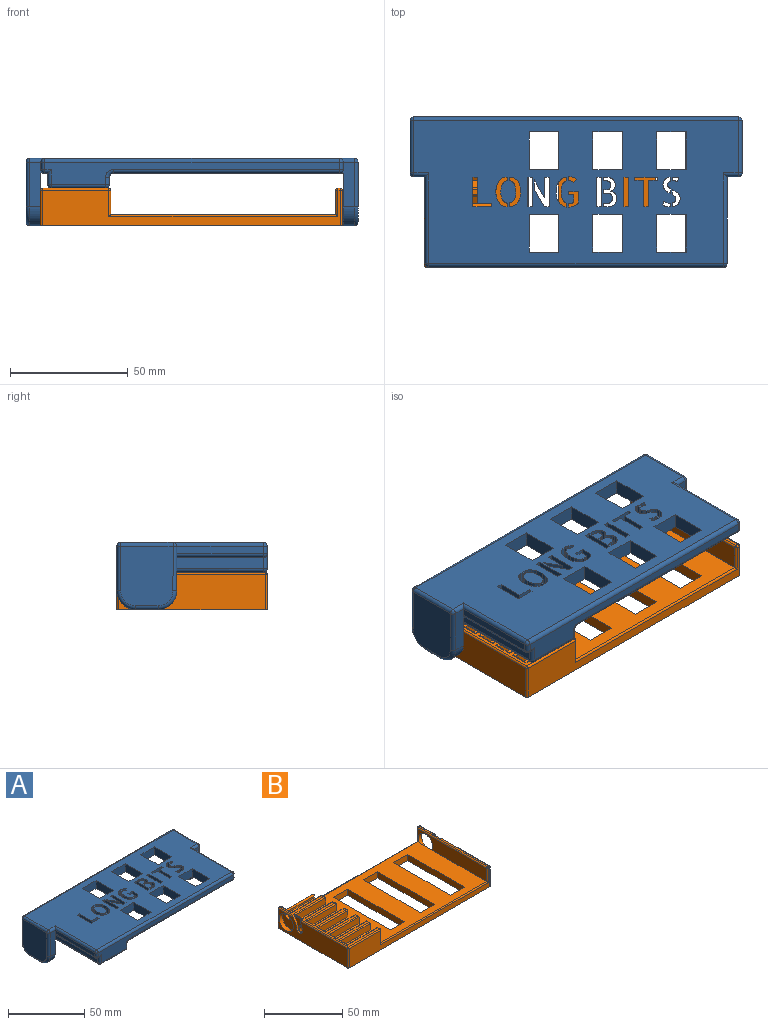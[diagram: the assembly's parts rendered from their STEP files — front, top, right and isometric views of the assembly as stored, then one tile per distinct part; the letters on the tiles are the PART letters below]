
ASSEMBLY  parts=2 mates=1
PART A: 304 faces, bbox 141x64.4x29.2 mm
  f0: plane 137.8x60.58mm, normal (0,0,1), area 6261.5mm2, adj f47,f48,f57,f58,f61,f64,f65,f66
  f1: plane 97.67x60.58mm, normal (0,0,-1), area 4295.3mm2, adj f4,f21,f26,f28,f70,f71,f73,f74
  f2: plane 57.78x23.02mm, normal (0,0,-1), area 1295.3mm2, adj f3,f13,f15,f17,f93,f94,f95,f96
  f3: cylinder r=1.59mm len=59.58mm, axis (0,1,0), area 145.3mm2, adj f2,f7,f12,f15,f18,f96,f97,f98
  f4: cylinder r=1.59mm len=60.58mm, axis (0,1,0), area 148.8mm2, adj f1,f7,f20,f72,f89,f90,f91,f92
  f5: plane 36.77x3.18mm, normal (1,0,0), area 116.7mm2, adj f28,f66,f68,f70
  f6: plane 36.77x3.18mm, normal (-1,0,0), area 116.7mm2, adj f25,f52,f60,f61
  f7: plane 61.05x3.18mm, normal (1,0,0), area 191.7mm2, adj f3,f4,f12,f19,f72
  f8: plane 62.17x2.86mm, normal (0,0,-1), area 119.3mm2, adj f9,f11,f22,f25,f51,f52
  f9: plane 137.8x19.05mm, normal (0,1,0), area 634.3mm2, adj f8,f12,f22,f26,f37,f38,f42,f48
  f10: plane 125.1x9.53mm, normal (0,-1,0), area 545.5mm2, adj f14,f17,f19,f20,f21,f51,f60,f65
  f11: plane 62.17x4.76mm, normal (-1,0,0), area 289.9mm2, adj f8,f12,f13,f14
  f12: plane 26.21x5.53mm, normal (0,0.88,-0.48), area 163.6mm2, adj f3,f7,f9,f11,f13,f15,f72
  f13: cylinder r=1.59mm len=59.58mm, axis (0,-1,0), area 146.7mm2, adj f2,f11,f12,f15,f16
  f14: cylinder r=1.59mm len=6.35mm, axis (0,0,-1), area 13.3mm2, adj f10,f11,f16,f51
  f15: cylinder r=1.59mm len=25.81mm, axis (-1,0,0), area 41.9mm2, adj f2,f3,f12,f13
  f16: sphere r=1.59mm, area 4mm2, adj f13,f14,f17
  f17: cylinder r=1.59mm len=23.02mm, axis (1,0,0), area 57.4mm2, adj f2,f10,f16,f18
  f18: sphere r=1.59mm, area 4mm2, adj f3,f17,f19
  f19: cylinder r=1.59mm len=3.18mm, axis (0,0,1), area 7.9mm2, adj f7,f10,f18,f20
  f20: torus R=3.17mm, axis (0,1,0), area 8.5mm2, adj f4,f10,f19,f21
  f21: cylinder r=1.59mm len=96.05mm, axis (1,0,0), area 239.5mm2, adj f1,f10,f20,f69
  f22: plane 25.4x22.23mm, normal (1,0,0), area 400.5mm2, adj f8,f9,f23,f25,f30,f32,f38,f39
  f23: plane 9.53x4.76mm, normal (0,0,-1), area 45.4mm2, adj f22,f38,f39,f41
  f24: plane 25.4x22.23mm, normal (-1,0,0), area 547.2mm2, adj f40,f41,f42,f43,f46,f47
  f25: plane 19.05x6.35mm, normal (0,-1,0), area 91.3mm2, adj f6,f8,f22,f39,f46,f52,f57
  f26: plane 25.4x23.81mm, normal (-1,0,0), area 401mm2, adj f1,f9,f27,f28,f33,f35,f36,f37
  f27: plane 9.53x4.76mm, normal (0,0,-1), area 45.4mm2, adj f26,f36,f37,f50
  f28: plane 19.05x6.35mm, normal (0,-1,0), area 91.3mm2, adj f1,f5,f26,f36,f59,f64,f70
  f29: plane 25.4x22.23mm, normal (1,0,0), area 547.2mm2, adj f45,f49,f50,f55,f58,f59
  f30: cylinder r=6.1mm len=12.19mm, axis (-1,0,0), area 107mm2, adj f22,f31
  f31: plane 12.19x12.19mm, normal (1,0,0), area 116.7mm2, adj f30
  f32: sphere r=2.54mm, area 40.5mm2, adj f22
  f33: cylinder r=6.1mm len=12.19mm, axis (1,0,0), area 107mm2, adj f26,f34
  f34: plane 12.19x12.19mm, normal (-1,0,0), area 116.7mm2, adj f33
  f35: sphere r=2.54mm, area 40.5mm2, adj f26
  f36: cylinder r=7.94mm len=7.94mm, axis (1,0,0), area 59.4mm2, adj f26,f27,f28,f55
  f37: cylinder r=7.94mm len=7.94mm, axis (1,0,0), area 59.4mm2, adj f9,f26,f27,f45
  f38: cylinder r=7.94mm len=7.94mm, axis (-1,0,0), area 59.4mm2, adj f9,f22,f23,f40
  f39: cylinder r=7.94mm len=7.94mm, axis (1,0,0), area 59.4mm2, adj f22,f23,f25,f43
  f40: torus R=6.35mm, axis (-1,0,0), area 28.8mm2, adj f24,f38,f41,f42
  f41: cylinder r=1.59mm len=9.53mm, axis (0,-1,0), area 23.8mm2, adj f23,f24,f40,f43
  f42: cylinder r=1.59mm len=19.05mm, axis (0,0,1), area 47.5mm2, adj f9,f24,f40,f44
  f43: torus R=6.35mm, axis (-1,0,0), area 28.8mm2, adj f24,f39,f41,f46
  f44: sphere r=1.59mm, area 4mm2, adj f42,f47,f48
  f45: torus R=6.35mm, axis (-1,0,0), area 28.8mm2, adj f29,f37,f49,f50
  f46: cylinder r=1.59mm len=19.05mm, axis (0,0,-1), area 47.5mm2, adj f24,f25,f43,f53
  f47: cylinder r=1.59mm len=22.23mm, axis (0,-1,0), area 55.4mm2, adj f0,f24,f44,f53
  f48: cylinder r=1.59mm len=137.8mm, axis (1,0,0), area 343.6mm2, adj f0,f9,f44,f54
  f49: cylinder r=1.59mm len=19.05mm, axis (0,0,-1), area 47.5mm2, adj f9,f29,f45,f54
  f50: cylinder r=1.59mm len=9.53mm, axis (0,1,0), area 23.8mm2, adj f27,f29,f45,f55
  f51: cylinder r=1.59mm len=2.86mm, axis (1,0,0), area 4.6mm2, adj f8,f10,f14,f56
  f52: cylinder r=1.59mm len=36.77mm, axis (0,-1,0), area 91.7mm2, adj f6,f8,f25,f56
  f53: sphere r=1.59mm, area 4mm2, adj f46,f47,f57
  f54: sphere r=1.59mm, area 4mm2, adj f48,f49,f58
  f55: torus R=6.35mm, axis (-1,0,0), area 28.8mm2, adj f29,f36,f50,f59
  f56: sphere r=1.59mm, area 4mm2, adj f51,f52,f60
  f57: cylinder r=1.59mm len=6.35mm, axis (1,0,0), area 13.3mm2, adj f0,f25,f53,f61
  f58: cylinder r=1.59mm len=22.23mm, axis (0,1,0), area 55.4mm2, adj f0,f29,f54,f62
  f59: cylinder r=1.59mm len=19.05mm, axis (0,0,-1), area 47.5mm2, adj f28,f29,f55,f62
  f60: cylinder r=1.59mm len=3.18mm, axis (0,0,-1), area 7.9mm2, adj f6,f10,f56,f63
  f61: cylinder r=1.59mm len=38.35mm, axis (0,1,0), area 93.1mm2, adj f0,f6,f57,f63
  f62: sphere r=1.59mm, area 4mm2, adj f58,f59,f64
  f63: sphere r=1.59mm, area 4mm2, adj f60,f61,f65
  f64: cylinder r=1.59mm len=6.35mm, axis (1,0,0), area 13.3mm2, adj f0,f28,f62,f66
  f65: cylinder r=1.59mm len=125.1mm, axis (-1,0,0), area 312mm2, adj f0,f10,f63,f67
  f66: cylinder r=1.59mm len=38.35mm, axis (0,-1,0), area 93.1mm2, adj f0,f5,f64,f67
  f67: sphere r=1.59mm, area 4mm2, adj f65,f66,f68
  f68: cylinder r=1.59mm len=3.18mm, axis (0,0,1), area 7.9mm2, adj f5,f10,f67,f69
  f69: sphere r=1.59mm, area 4mm2, adj f21,f68,f70
  f70: cylinder r=1.59mm len=36.77mm, axis (0,1,0), area 91.7mm2, adj f1,f5,f28,f69
  f71: cylinder r=1.59mm len=97.64mm, axis (-1,0,0), area 243.5mm2, adj f1,f9,f26,f72
  f72: torus R=3.17mm, axis (0,1,0), area 6.8mm2, adj f4,f7,f9,f12,f71
  f73: extruded ~6.35x1.58mm, area 12.9mm2, adj f0,f1,f74,f89
  f74: extruded ~6.35x1.29mm, area 8.6mm2, adj f0,f1,f73,f75
  f75: plane 6.35x0.68mm, normal (0,1,0), area 4.3mm2, adj f0,f1,f74,f76
  f76: plane 6.35x1.62mm, normal (-1,0,0), area 10.3mm2, adj f0,f1,f75,f77
  f77: extruded ~6.35x1.08mm, area 7.3mm2, adj f0,f1,f76,f78
  f78: extruded ~6.35x0.9mm, area 8.1mm2, adj f0,f1,f77,f79
  f79: extruded ~6.35x1.46mm, area 10.1mm2, adj f0,f1,f78,f80
  f80: extruded ~6.35x2.09mm, area 13.4mm2, adj f0,f1,f79,f81
  f81: extruded ~6.35x2.09mm, area 13.4mm2, adj f0,f1,f80,f82
  f82: extruded ~6.35x1.45mm, area 10mm2, adj f0,f1,f81,f83
  f83: extruded ~6.35x0.9mm, area 8mm2, adj f0,f1,f82,f84
  f84: extruded ~6.35x1.1mm, area 7.4mm2, adj f0,f1,f83,f85
  f85: plane 6.35x1.54mm, normal (-1,0,0), area 9.8mm2, adj f0,f1,f84,f86
  f86: plane 6.35x1.11mm, normal (0,-1,0), area 7.1mm2, adj f0,f1,f85,f87
  f87: extruded ~6.35x0.86mm, area 5.8mm2, adj f0,f1,f86,f88
  f88: extruded ~6.35x1.57mm, area 12.9mm2, adj f0,f1,f87,f90
  f89: extruded ~6.36x2.01mm, area 14.4mm2, adj f0,f1,f4,f73,f92
  f90: extruded ~6.36x2mm, area 14.4mm2, adj f0,f1,f4,f88,f91
  f91: extruded ~6.44x2.71mm, area 17.6mm2, adj f0,f4,f90,f92
  f92: extruded ~6.44x2.72mm, area 17.7mm2, adj f0,f4,f89,f91
  f93: plane 12.7x11.13mm, normal (-1,0,0), area 141.3mm2, adj f0,f2,f94,f97
  f94: plane 12.7x2.1mm, normal (0,-1,0), area 26.7mm2, adj f0,f2,f93,f95
  f95: plane 12.7x12.69mm, normal (1,0,0), area 161.2mm2, adj f0,f2,f94,f96
  f96: plane 12.7x7.94mm, normal (0,1,0), area 100.8mm2, adj f0,f2,f3,f95,f98
  f97: plane 12.7x5.84mm, normal (0,-1,0), area 74.1mm2, adj f0,f2,f3,f93,f98
  f98: plane 12.48x1.57mm, normal (-1,0,0), area 19.6mm2, adj f0,f3,f96,f97
  f99: plane 12.69x6.35mm, normal (-1,0,0), area 80.6mm2, adj f0,f1,f100,f105
  f100: plane 6.35x2.1mm, normal (0,-1,0), area 13.3mm2, adj f0,f1,f99,f101
  f101: plane 8.75x6.35mm, normal (1,0,0), area 55.6mm2, adj f0,f1,f100,f102
  f102: plane 7.53x6.35mm, normal (-0.87,-0.49,0), area 55mm2, adj f0,f1,f101,f103
  f103: plane 6.35x3.96mm, normal (1,0,0), area 25.2mm2, adj f0,f1,f102,f104
  f104: plane 7.51x6.35mm, normal (0.87,0.49,0), area 54.9mm2, adj f0,f1,f103,f105
  f105: plane 6.35x2.1mm, normal (0,1,0), area 13.3mm2, adj f0,f1,f99,f104
  f106: extruded ~6.35x0.43mm, area 2.7mm2, adj f0,f1,f107,f144
  f107: extruded ~6.35x0.75mm, area 4.9mm2, adj f0,f1,f106,f108
  f108: extruded ~6.35x0.88mm, area 6mm2, adj f0,f1,f107,f109
  f109: extruded ~6.35x0.84mm, area 6.7mm2, adj f0,f1,f108,f110
  f110: extruded ~6.35x1.03mm, area 7.7mm2, adj f0,f1,f109,f111
  f111: extruded ~6.35x1.48mm, area 9.6mm2, adj f0,f1,f110,f112
  f112: extruded ~6.35x1.25mm, area 8.2mm2, adj f0,f1,f111,f113
  f113: extruded ~6.35x0.92mm, area 7.2mm2, adj f0,f1,f112,f114
  f114: extruded ~6.35x0.84mm, area 6.5mm2, adj f0,f1,f113,f115
  f115: extruded ~6.35x0.84mm, area 5.6mm2, adj f0,f1,f114,f116
  f116: extruded ~6.35x0.65mm, area 4.5mm2, adj f0,f1,f115,f117
  f117: extruded ~6.35x0.59mm, area 5.1mm2, adj f0,f1,f116,f118
  f118: extruded ~6.35x0.77mm, area 5.6mm2, adj f0,f1,f117,f119
  f119: extruded ~6.35x0.97mm, area 6.3mm2, adj f0,f1,f118,f120
  f120: extruded ~6.35x1.58mm, area 10.4mm2, adj f0,f1,f119,f121
  f121: extruded ~6.35x1.08mm, area 9.1mm2, adj f0,f1,f120,f122
  f122: extruded ~6.35x1.34mm, area 9.4mm2, adj f0,f1,f121,f123
  f123: extruded ~6.35x1.57mm, area 10.1mm2, adj f0,f1,f122,f124
  f124: plane 6.35x0.88mm, normal (0,-1,0), area 5.6mm2, adj f0,f1,f123,f125
  f125: plane 6.35x1.57mm, normal (1,0,0), area 9.9mm2, adj f0,f1,f124,f126
  f126: plane 6.35x0.67mm, normal (0,1,0), area 4.3mm2, adj f0,f1,f125,f127
  f127: extruded ~6.35x1.28mm, area 8.2mm2, adj f0,f1,f126,f128
  f128: extruded ~6.35x0.74mm, area 5.5mm2, adj f0,f1,f127,f129
  f129: extruded ~6.35x0.61mm, area 4.5mm2, adj f0,f1,f128,f130
  f130: extruded ~6.35x0.65mm, area 4.2mm2, adj f0,f1,f129,f131
  f131: extruded ~6.35x1.19mm, area 7.7mm2, adj f0,f1,f130,f132
  f132: extruded ~6.35x0.59mm, area 5.2mm2, adj f0,f1,f131,f133
  f133: extruded ~6.35x0.74mm, area 4.9mm2, adj f0,f1,f132,f134
  f134: extruded ~6.35x0.78mm, area 4.9mm2, adj f0,f1,f133,f135
  f135: plane 6.35x0.83mm, normal (0,-1,0), area 5.3mm2, adj f0,f1,f134,f136
  f136: plane 6.35x1.4mm, normal (1,0,0), area 8.9mm2, adj f0,f1,f135,f137
  f137: plane 6.35x1.72mm, normal (0,1,0), area 10.9mm2, adj f0,f1,f136,f138
  f138: extruded ~6.35x1.57mm, area 11.1mm2, adj f0,f1,f137,f139
  f139: extruded ~6.35x1.57mm, area 10.7mm2, adj f0,f1,f138,f140
  f140: extruded ~6.35x1.57mm, area 10.7mm2, adj f0,f1,f139,f141
  f141: extruded ~6.35x1.43mm, area 10.1mm2, adj f0,f1,f140,f142
  f142: plane 6.35x1.88mm, normal (0,-1,0), area 11.9mm2, adj f0,f1,f141,f143
  f143: plane 6.35x1.52mm, normal (1,0,0), area 9.6mm2, adj f0,f1,f142,f144
  f144: plane 6.35x2mm, normal (0,1,0), area 12.7mm2, adj f0,f1,f106,f143
  f145: extruded ~6.35x0.89mm, area 7.7mm2, adj f0,f1,f146,f159
  f146: plane 6.35x4.91mm, normal (-1,0,0), area 31.2mm2, adj f0,f1,f145,f147
  f147: plane 6.35x4.2mm, normal (0,-1,0), area 26.7mm2, adj f0,f1,f146,f148
  f148: plane 6.35x1.41mm, normal (1,0,0), area 9mm2, adj f0,f1,f147,f149
  f149: plane 6.35x2.16mm, normal (0,1,0), area 13.7mm2, adj f0,f1,f148,f150
  f150: plane 6.35x3.14mm, normal (1,0,0), area 19.9mm2, adj f0,f1,f149,f151
  f151: extruded ~6.35x0.42mm, area 3.3mm2, adj f0,f1,f150,f152
  f152: extruded ~6.35x0.6mm, area 4mm2, adj f0,f1,f151,f153
  f153: extruded ~6.35x0.62mm, area 4mm2, adj f0,f1,f152,f154
  f154: extruded ~6.35x0.51mm, area 3.2mm2, adj f0,f1,f153,f155
  f155: plane 6.35x1.52mm, normal (1,0,0), area 9.6mm2, adj f0,f1,f154,f156
  f156: plane 6.35x0.02mm, normal (0,1,0), area 0.1mm2, adj f0,f1,f155,f157
  f157: extruded ~6.35x1.15mm, area 7.3mm2, adj f0,f1,f156,f158
  f158: extruded ~6.35x1.12mm, area 7.4mm2, adj f0,f1,f157,f159
  f159: extruded ~6.35x1.03mm, area 7.4mm2, adj f0,f1,f145,f158
  f160: extruded ~6.35x1.4mm, area 9.5mm2, adj f0,f1,f161,f179
  f161: extruded ~6.35x0.9mm, area 7.6mm2, adj f0,f1,f160,f162
  f162: extruded ~6.35x0.96mm, area 6.8mm2, adj f0,f1,f161,f163
  f163: plane 6.35x1.59mm, normal (-1,0,0), area 10.1mm2, adj f0,f1,f162,f164
  f164: plane 6.35x0.7mm, normal (0,-1,0), area 4.4mm2, adj f0,f1,f163,f165
  f165: extruded ~6.35x1.13mm, area 7.7mm2, adj f0,f1,f164,f166
  f166: extruded ~6.35x1.45mm, area 12.3mm2, adj f0,f1,f165,f167
  f167: extruded ~6.35x1.95mm, area 13.8mm2, adj f0,f1,f166,f168
  f168: extruded ~6.35x2.63mm, area 16.9mm2, adj f0,f1,f167,f169
  f169: extruded ~6.35x2.63mm, area 16.9mm2, adj f0,f1,f168,f170
  f170: extruded ~6.35x1.96mm, area 13.9mm2, adj f0,f1,f169,f171
  f171: extruded ~6.35x1.45mm, area 12.4mm2, adj f0,f1,f170,f172
  f172: extruded ~6.35x1.49mm, area 10.1mm2, adj f0,f1,f171,f173
  f173: extruded ~6.35x0.33mm, area 2.2mm2, adj f0,f1,f172,f174
  f174: plane 6.35x1.57mm, normal (-1,0,0), area 10mm2, adj f0,f1,f173,f175
  f175: extruded ~6.35x0.96mm, area 6.9mm2, adj f0,f1,f174,f176
  f176: extruded ~6.35x0.97mm, area 7.9mm2, adj f0,f1,f175,f177
  f177: extruded ~6.35x1.46mm, area 9.9mm2, adj f0,f1,f176,f178
  f178: extruded ~6.35x1.96mm, area 12.6mm2, adj f0,f1,f177,f179
  f179: extruded ~6.35x1.94mm, area 12.4mm2, adj f0,f1,f160,f178
  f180: plane 6.35x1.7mm, normal (1,0,0), area 10.8mm2, adj f0,f1,f181,f188
  f181: plane 6.35x0.07mm, normal (0,1,0), area 0.4mm2, adj f0,f1,f180,f182
  f182: extruded ~6.35x1.1mm, area 7.2mm2, adj f0,f1,f181,f183
  f183: extruded ~6.35x0.95mm, area 7.6mm2, adj f0,f1,f182,f184
  f184: plane 6.35x1.43mm, normal (-0.66,0.75,0), area 12.2mm2, adj f0,f1,f183,f185
  f185: extruded ~6.35x1.6mm, area 12.2mm2, adj f0,f1,f184,f186
  f186: extruded ~6.35x0.43mm, area 2.9mm2, adj f0,f1,f185,f187
  f187: extruded ~6.35x1.5mm, area 9.6mm2, adj f0,f1,f186,f188
  f188: plane 6.35x0.02mm, normal (0,-1,0), area 0.1mm2, adj f0,f1,f180,f187
  f189: plane 12.69x6.35mm, normal (1,0,0), area 80.6mm2, adj f0,f1,f190,f192
  f190: plane 6.35x2.1mm, normal (0,1,0), area 13.4mm2, adj f0,f1,f189,f191
  f191: plane 12.69x6.35mm, normal (-1,0,0), area 80.6mm2, adj f0,f1,f190,f192
  f192: plane 6.35x2.1mm, normal (0,-1,0), area 13.4mm2, adj f0,f1,f189,f191
  f193: extruded ~6.35x1.1mm, area 7.4mm2, adj f0,f1,f194,f212
  f194: plane 6.35x1.62mm, normal (1,0,0), area 10.3mm2, adj f0,f1,f193,f195
  f195: plane 6.35x0.68mm, normal (0,1,0), area 4.3mm2, adj f0,f1,f194,f196
  f196: extruded ~6.35x1.28mm, area 8.6mm2, adj f0,f1,f195,f197
  f197: extruded ~6.35x1.56mm, area 12.8mm2, adj f0,f1,f196,f198
  f198: extruded ~6.35x2.01mm, area 14.4mm2, adj f0,f1,f197,f199
  f199: extruded ~6.35x2.72mm, area 17.5mm2, adj f0,f1,f198,f200
  f200: extruded ~6.35x2.71mm, area 17.5mm2, adj f0,f1,f199,f201
  f201: extruded ~6.35x2mm, area 14.4mm2, adj f0,f1,f200,f202
  f202: extruded ~6.35x1.57mm, area 12.9mm2, adj f0,f1,f201,f203
  f203: extruded ~6.35x0.82mm, area 5.6mm2, adj f0,f1,f202,f204
  f204: plane 6.35x1.14mm, normal (0,-1,0), area 7.2mm2, adj f0,f1,f203,f205
  f205: plane 6.35x1.52mm, normal (1,0,0), area 9.7mm2, adj f0,f1,f204,f206
  f206: extruded ~6.35x1.08mm, area 7.3mm2, adj f0,f1,f205,f207
  f207: extruded ~6.35x0.91mm, area 8.1mm2, adj f0,f1,f206,f208
  f208: extruded ~6.35x1.45mm, area 10mm2, adj f0,f1,f207,f209
  f209: extruded ~6.35x2.09mm, area 13.4mm2, adj f0,f1,f208,f210
  f210: extruded ~6.35x2.09mm, area 13.4mm2, adj f0,f1,f209,f211
  f211: extruded ~6.35x1.45mm, area 10mm2, adj f0,f1,f210,f212
  f212: extruded ~6.35x0.9mm, area 8mm2, adj f0,f1,f193,f211
  f213: extruded ~6.35x1.02mm, area 8.3mm2, adj f0,f1,f214,f226
  f214: extruded ~6.35x1.08mm, area 8.2mm2, adj f0,f1,f213,f215
  f215: extruded ~6.35x1.16mm, area 8.2mm2, adj f0,f1,f214,f216
  f216: plane 6.35x2.02mm, normal (1,0,0), area 12.8mm2, adj f0,f1,f215,f217
  f217: extruded ~6.35x1.02mm, area 8mm2, adj f0,f1,f216,f218
  f218: extruded ~6.35x1mm, area 7mm2, adj f0,f1,f217,f219
  f219: extruded ~6.35x1.88mm, area 16.3mm2, adj f0,f1,f218,f220
  f220: plane 6.35x1.64mm, normal (1,0,0), area 10.4mm2, adj f0,f1,f219,f221
  f221: plane 6.35x0.12mm, normal (0,1,0), area 0.7mm2, adj f0,f1,f220,f222
  f222: extruded ~6.35x1.29mm, area 8.7mm2, adj f0,f1,f221,f223
  f223: extruded ~6.35x1.04mm, area 8.4mm2, adj f0,f1,f222,f224
  f224: extruded ~6.35x1.06mm, area 8mm2, adj f0,f1,f223,f225
  f225: extruded ~6.35x1.21mm, area 7.8mm2, adj f0,f1,f224,f226
  f226: extruded ~6.35x1.5mm, area 9.8mm2, adj f0,f1,f213,f225
  f227: extruded ~6.35x0.91mm, area 7.3mm2, adj f0,f1,f228,f241
  f228: plane 6.35x1.66mm, normal (-1,0,0), area 10.5mm2, adj f0,f1,f227,f229
  f229: plane 6.35x0.71mm, normal (0,-1,0), area 4.5mm2, adj f0,f1,f228,f230
  f230: extruded ~6.35x0.54mm, area 3.7mm2, adj f0,f1,f229,f231
  f231: extruded ~6.35x1.03mm, area 8.1mm2, adj f0,f1,f230,f232
  f232: extruded ~6.35x1.06mm, area 8.1mm2, adj f0,f1,f231,f233
  f233: extruded ~6.35x1.36mm, area 8.9mm2, adj f0,f1,f232,f234
  f234: extruded ~6.35x1.36mm, area 8.9mm2, adj f0,f1,f233,f235
  f235: extruded ~6.35x1mm, area 8mm2, adj f0,f1,f234,f236
  f236: extruded ~6.35x1.03mm, area 8.1mm2, adj f0,f1,f235,f237
  f237: extruded ~6.35x1.14mm, area 8.2mm2, adj f0,f1,f236,f238
  f238: plane 6.35x1.97mm, normal (-1,0,0), area 12.5mm2, adj f0,f1,f237,f239
  f239: extruded ~6.35x0.91mm, area 7.4mm2, adj f0,f1,f238,f240
  f240: extruded ~6.35x1.09mm, area 7.4mm2, adj f0,f1,f239,f241
  f241: extruded ~6.35x0.96mm, area 6.6mm2, adj f0,f1,f227,f240
  f242: extruded ~6.35x0.49mm, area 3.5mm2, adj f0,f1,f243,f252
  f243: extruded ~6.35x1.08mm, area 7.4mm2, adj f0,f1,f242,f244
  f244: plane 6.35x1.73mm, normal (0,-1,0), area 11mm2, adj f0,f1,f243,f245
  f245: plane 6.35x1.54mm, normal (1,0,0), area 9.8mm2, adj f0,f1,f244,f246
  f246: extruded ~6.35x0.88mm, area 5.6mm2, adj f0,f1,f245,f247
  f247: extruded ~6.35x0.57mm, area 3.7mm2, adj f0,f1,f246,f248
  f248: extruded ~6.35x0.34mm, area 2.4mm2, adj f0,f1,f247,f249
  f249: extruded ~6.35x0.21mm, area 1.5mm2, adj f0,f1,f248,f250
  f250: extruded ~6.35x0.17mm, area 1.3mm2, adj f0,f1,f249,f251
  f251: extruded ~6.35x0.39mm, area 2.8mm2, adj f0,f1,f250,f252
  f252: extruded ~6.35x0.5mm, area 3.6mm2, adj f0,f1,f242,f251
  f253: extruded ~6.35x0.79mm, area 5.2mm2, adj f0,f1,f254,f263
  f254: extruded ~6.35x0.77mm, area 5.1mm2, adj f0,f1,f253,f255
  f255: extruded ~6.35x0.61mm, area 4.2mm2, adj f0,f1,f254,f256
  f256: plane 6.35x1.48mm, normal (0.97,-0.24,0), area 9.7mm2, adj f0,f1,f255,f257
  f257: extruded ~6.35x0.7mm, area 5.3mm2, adj f0,f1,f256,f258
  f258: extruded ~6.35x0.85mm, area 5.7mm2, adj f0,f1,f257,f259
  f259: extruded ~6.35x0.66mm, area 4.3mm2, adj f0,f1,f258,f260
  f260: plane 6.35x1.12mm, normal (0,1,0), area 7.1mm2, adj f0,f1,f259,f261
  f261: plane 6.35x1.57mm, normal (-1,0,0), area 10mm2, adj f0,f1,f260,f262
  f262: plane 6.35x0.05mm, normal (0,-1,0), area 0.3mm2, adj f0,f1,f261,f263
  f263: extruded ~6.35x0.74mm, area 4.7mm2, adj f0,f1,f253,f262
  f264: plane 11.28x6.35mm, normal (-1,0,0), area 71.6mm2, adj f0,f1,f265,f271
  f265: plane 6.35x3.79mm, normal (0,1,0), area 24.1mm2, adj f0,f1,f264,f266
  f266: plane 6.35x1.41mm, normal (-1,0,0), area 9mm2, adj f0,f1,f265,f267
  f267: plane 9.66x6.35mm, normal (0,-1,0), area 61.4mm2, adj f0,f1,f266,f268
  f268: plane 6.35x1.41mm, normal (1,0,0), area 9mm2, adj f0,f1,f267,f269
  f269: plane 6.35x3.79mm, normal (0,1,0), area 24.1mm2, adj f0,f1,f268,f270
  f270: plane 11.28x6.35mm, normal (1,0,0), area 71.6mm2, adj f0,f1,f269,f271
  f271: plane 6.35x2.08mm, normal (0,1,0), area 13.2mm2, adj f0,f1,f264,f270
  f272: plane 6.35x2.1mm, normal (0,1,0), area 13.3mm2, adj f0,f1,f273,f275
  f273: plane 12.69x6.35mm, normal (-1,0,0), area 80.6mm2, adj f0,f1,f272,f274
  f274: plane 6.35x2.1mm, normal (0,-1,0), area 13.3mm2, adj f0,f1,f273,f275
  f275: plane 12.69x6.35mm, normal (1,0,0), area 80.6mm2, adj f0,f1,f272,f274
  f276: plane 12.69x6.35mm, normal (-1,0,0), area 80.6mm2, adj f0,f1,f277,f279
  f277: plane 6.35x2.07mm, normal (0,-1,0), area 13.1mm2, adj f0,f1,f276,f278
  f278: plane 12.69x6.35mm, normal (1,0,0), area 80.6mm2, adj f0,f1,f277,f279
  f279: plane 6.35x2.07mm, normal (0,1,0), area 13.1mm2, adj f0,f1,f276,f278
  f280: plane 16.01x6.35mm, normal (-1,0,0), area 101.6mm2, adj f0,f1,f281,f283
  f281: plane 12.7x6.35mm, normal (0,-1,0), area 80.6mm2, adj f0,f1,f280,f282
  f282: plane 16.01x6.35mm, normal (1,0,0), area 101.6mm2, adj f0,f1,f281,f283
  f283: plane 12.7x6.35mm, normal (0,1,0), area 80.6mm2, adj f0,f1,f280,f282
  f284: plane 12.7x6.35mm, normal (0,-1,0), area 80.6mm2, adj f0,f1,f285,f287
  f285: plane 16.01x6.35mm, normal (1,0,0), area 101.6mm2, adj f0,f1,f284,f286
  f286: plane 12.7x6.35mm, normal (0,1,0), area 80.6mm2, adj f0,f1,f285,f287
  f287: plane 16.01x6.35mm, normal (-1,0,0), area 101.6mm2, adj f0,f1,f284,f286
  f288: plane 16.01x6.35mm, normal (-1,0,0), area 101.6mm2, adj f0,f1,f289,f291
  f289: plane 12.7x6.35mm, normal (0,-1,0), area 80.6mm2, adj f0,f1,f288,f290
  f290: plane 16.01x6.35mm, normal (1,0,0), area 101.6mm2, adj f0,f1,f289,f291
  f291: plane 12.7x6.35mm, normal (0,1,0), area 80.6mm2, adj f0,f1,f288,f290
  f292: plane 12.7x6.35mm, normal (0,-1,0), area 80.6mm2, adj f0,f1,f293,f295
  f293: plane 16x6.35mm, normal (1,0,0), area 101.6mm2, adj f0,f1,f292,f294
  f294: plane 12.7x6.35mm, normal (0,1,0), area 80.6mm2, adj f0,f1,f293,f295
  f295: plane 16x6.35mm, normal (-1,0,0), area 101.6mm2, adj f0,f1,f292,f294
  f296: plane 12.7x6.35mm, normal (0,1,0), area 80.6mm2, adj f0,f1,f297,f299
  f297: plane 16x6.35mm, normal (-1,0,0), area 101.6mm2, adj f0,f1,f296,f298
  f298: plane 12.7x6.35mm, normal (0,-1,0), area 80.6mm2, adj f0,f1,f297,f299
  f299: plane 16x6.35mm, normal (1,0,0), area 101.6mm2, adj f0,f1,f296,f298
  f300: plane 16x6.35mm, normal (-1,0,0), area 101.6mm2, adj f0,f1,f301,f303
  f301: plane 12.7x6.35mm, normal (0,-1,0), area 80.6mm2, adj f0,f1,f300,f302
  f302: plane 16x6.35mm, normal (1,0,0), area 101.6mm2, adj f0,f1,f301,f303
  f303: plane 12.7x6.35mm, normal (0,1,0), area 80.6mm2, adj f0,f1,f300,f302
PART B: 120 faces, bbox 128.3x63.8x15.9 mm
  f0: plane 62.17x28.26mm, normal (0,0,1), area 376.7mm2, adj f14,f15,f17,f84,f88,f90,f91,f92
  f1: plane 26.8x1.36mm, normal (0,-1,0), area 36.4mm2, adj f2,f10,f45,f119
  f2: plane 62.96x11.11mm, normal (1,0,0), area 403.6mm2, adj f1,f4,f13,f27,f29,f30,f32,f33
  f3: plane 128.28x63.75mm, normal (0,0,-1), area 6232.4mm2, adj f8,f11,f12,f13,f56,f57,f58,f59
  f4: plane 95.57x62.17mm, normal (0,0,1), area 3994.2mm2, adj f2,f5,f6,f28,f56,f57,f58,f59
  f5: cylinder r=6.35mm len=12.7mm, axis (1,0,0), area 116.5mm2, adj f4,f6,f12,f28
  f6: plane 11x3.18mm, normal (1,0,0), area 24.8mm2, adj f4,f5
  f7: plane 62.17x1.27mm, normal (0,0,1), area 75.6mm2, adj f20,f21,f22,f70,f74,f75,f79,f80
  f8: plane 126.69x15.08mm, normal (0,-1,0), area 830.9mm2, adj f3,f76,f80,f82,f83,f85,f87,f88
  f9: cylinder r=6.35mm len=12.7mm, axis (-1,0,0), area 119.9mm2, adj f10,f11,f26,f27,f36,f37,f46,f119
  f10: plane 12.7x12.34mm, normal (-1,0,0), area 95.6mm2, adj f1,f9,f27,f36,f44,f45,f46,f119
  f11: plane 62.17x15.08mm, normal (-1,0,0), area 761.6mm2, adj f3,f9,f15,f16,f17,f83,f84,f111
  f12: plane 62.17x15.08mm, normal (1,0,0), area 761.6mm2, adj f3,f5,f21,f22,f23,f69,f70,f75
  f13: plane 126.69x15.08mm, normal (0,1,0), area 625.4mm2, adj f2,f3,f68,f69,f71,f73,f74,f112
  f14: plane 10.48x9.47mm, normal (-1,0,0), area 35.4mm2, adj f0,f15,f16,f17,f19
  f15: cylinder r=9.37mm len=7.94mm, axis (-1,0,0), area 11.8mm2, adj f0,f11,f14,f16,f111
  f16: cylinder r=2.54mm len=5.08mm, axis (-1,0,0), area 10.1mm2, adj f11,f14,f15,f17
  f17: cylinder r=14.45mm len=7.94mm, axis (-1,0,0), area 10.5mm2, adj f0,f11,f14,f16,f84
  f18: sphere r=2.54mm, area 16.9mm2, adj f19
  f19: torus R=2.48mm, axis (-1,0,0), area 6.8mm2, adj f14,f18
  f20: plane 10.48x9.47mm, normal (1,0,0), area 35.4mm2, adj f7,f21,f22,f23,f25
  f21: cylinder r=9.37mm len=7.94mm, axis (1,0,0), area 11.8mm2, adj f7,f12,f20,f23,f70
  f22: cylinder r=14.45mm len=7.94mm, axis (1,0,0), area 10.5mm2, adj f7,f12,f20,f23,f75
  f23: cylinder r=2.54mm len=5.08mm, axis (1,0,0), area 10.1mm2, adj f12,f20,f21,f22
  f24: sphere r=2.54mm, area 16.9mm2, adj f25
  f25: torus R=2.48mm, axis (1,0,0), area 6.8mm2, adj f20,f24
  f26: plane 9.26x4.64mm, normal (1,0,0), area 16.8mm2, adj f9,f27,f68,f115,f118,f119
  f27: plane 26.99x4.93mm, normal (0,1,0), area 132.2mm2, adj f2,f9,f10,f26,f44,f113
  f28: plane 62.17x10.32mm, normal (-1,0,0), area 539.6mm2, adj f4,f5,f73,f79,f82
  f29: plane 26.99x4.93mm, normal (0,1,0), area 132.9mm2, adj f2,f31,f54,f99
  f30: plane 26.99x4.93mm, normal (0,-1,0), area 132.9mm2, adj f2,f31,f55,f101
  f31: plane 6.83x6.6mm, normal (1,0,0), area 38.8mm2, adj f29,f30,f54,f55,f100
  f32: plane 26.99x4.93mm, normal (0,1,0), area 132.9mm2, adj f2,f34,f52,f103
  f33: plane 26.99x4.93mm, normal (0,-1,0), area 132.9mm2, adj f2,f34,f53,f105
  f34: plane 6.83x6.6mm, normal (1,0,0), area 38.8mm2, adj f32,f33,f52,f53,f104
  f35: plane 26.99x4.93mm, normal (0,1,0), area 132.9mm2, adj f2,f37,f47,f107
  f36: plane 26.99x4.93mm, normal (0,-1,0), area 132.8mm2, adj f2,f9,f10,f37,f46,f109
  f37: plane 6.83x6.6mm, normal (1,0,0), area 38.6mm2, adj f9,f35,f36,f46,f47,f108
  f38: plane 26.99x4.93mm, normal (0,1,0), area 132.9mm2, adj f2,f40,f50,f95
  f39: plane 26.99x4.93mm, normal (0,-1,0), area 132.9mm2, adj f2,f40,f51,f97
  f40: plane 6.83x6.6mm, normal (1,0,0), area 38.8mm2, adj f38,f39,f50,f51,f96
  f41: plane 26.99x4.93mm, normal (0,1,0), area 132.9mm2, adj f2,f43,f48,f91
  f42: plane 26.99x4.93mm, normal (0,-1,0), area 132.9mm2, adj f2,f43,f49,f93
  f43: plane 6.83x6.6mm, normal (1,0,0), area 38.8mm2, adj f41,f42,f48,f49,f92
  f44: plane 26.8x3.3mm, normal (0,0.5,0.87), area 102.2mm2, adj f2,f10,f27,f45
  f45: plane 26.8x3.3mm, normal (0,-0.5,0.87), area 102.2mm2, adj f1,f2,f10,f44
  f46: plane 26.99x3.3mm, normal (0,-0.5,0.87), area 102.8mm2, adj f2,f9,f10,f36,f37,f47
  f47: plane 26.99x3.3mm, normal (0,0.5,0.87), area 102.9mm2, adj f2,f35,f37,f46
  f48: plane 26.99x3.3mm, normal (0,0.5,0.87), area 102.9mm2, adj f2,f41,f43,f49
  f49: plane 26.99x3.3mm, normal (0,-0.5,0.87), area 102.9mm2, adj f2,f42,f43,f48
  f50: plane 26.99x3.3mm, normal (0,0.5,0.87), area 102.9mm2, adj f2,f38,f40,f51
  f51: plane 26.99x3.3mm, normal (0,-0.5,0.87), area 102.9mm2, adj f2,f39,f40,f50
  f52: plane 26.99x3.3mm, normal (0,0.5,0.87), area 102.9mm2, adj f2,f32,f34,f53
  f53: plane 26.99x3.3mm, normal (0,-0.5,0.87), area 102.9mm2, adj f2,f33,f34,f52
  f54: plane 26.99x3.3mm, normal (0,0.5,0.87), area 102.9mm2, adj f2,f29,f31,f55
  f55: plane 26.99x3.3mm, normal (0,-0.5,0.87), area 102.9mm2, adj f2,f30,f31,f54
  f56: plane 12.7x4.76mm, normal (0,-1,0), area 60.5mm2, adj f3,f4,f57,f59
  f57: plane 51.05x4.76mm, normal (1,0,0), area 243.1mm2, adj f3,f4,f56,f58
  f58: plane 12.7x4.76mm, normal (0,1,0), area 60.5mm2, adj f3,f4,f57,f59
  f59: plane 51.05x4.76mm, normal (-1,0,0), area 243.1mm2, adj f3,f4,f56,f58
  f60: plane 51.05x4.76mm, normal (-1,0,0), area 243.1mm2, adj f3,f4,f61,f63
  f61: plane 12.7x4.76mm, normal (0,-1,0), area 60.5mm2, adj f3,f4,f60,f62
  f62: plane 51.05x4.76mm, normal (1,0,0), area 243.1mm2, adj f3,f4,f61,f63
  f63: plane 12.7x4.76mm, normal (0,1,0), area 60.5mm2, adj f3,f4,f60,f62
  f64: plane 51.05x4.76mm, normal (-1,0,0), area 243.1mm2, adj f3,f4,f65,f67
  f65: plane 12.7x4.76mm, normal (0,-1,0), area 60.5mm2, adj f3,f4,f64,f66
  f66: plane 51.05x4.76mm, normal (1,0,0), area 243.1mm2, adj f3,f4,f65,f67
  f67: plane 12.7x4.76mm, normal (0,1,0), area 60.5mm2, adj f3,f4,f64,f66
  f68: cylinder r=6.35mm len=27.78mm, axis (1,0,0), area 145.4mm2, adj f2,f13,f26,f118,f119
  f69: cylinder r=0.79mm len=15.08mm, axis (0,0,-1), area 18.8mm2, adj f3,f12,f13,f72
  f70: cylinder r=0.79mm len=13.2mm, axis (0,-1,0), area 15.6mm2, adj f7,f12,f21,f72
  f71: cylinder r=0.79mm len=96.37mm, axis (1,0,0), area 119.5mm2, adj f2,f4,f13,f73
  f72: sphere r=0.79mm, area 1mm2, adj f69,f70,f74
  f73: cylinder r=0.79mm len=11.11mm, axis (0,0,1), area 13.2mm2, adj f13,f28,f71,f77
  f74: cylinder r=0.79mm len=1.27mm, axis (1,0,0), area 1.6mm2, adj f7,f13,f72,f77
  f75: cylinder r=0.79mm len=42.95mm, axis (0,-1,0), area 53.3mm2, adj f7,f12,f22,f78
  f76: cylinder r=0.79mm len=15.08mm, axis (0,0,1), area 18.8mm2, adj f3,f8,f12,f78
  f77: sphere r=0.79mm, area 1mm2, adj f73,f74,f79
  f78: sphere r=0.79mm, area 1mm2, adj f75,f76,f80
  f79: cylinder r=0.79mm len=62.17mm, axis (0,-1,0), area 77.5mm2, adj f7,f28,f77,f81
  f80: cylinder r=0.79mm len=1.27mm, axis (-1,0,0), area 1.6mm2, adj f7,f8,f78,f81
  f81: sphere r=0.79mm, area 1mm2, adj f79,f80,f82
  f82: cylinder r=0.79mm len=11.11mm, axis (0,0,-1), area 13.2mm2, adj f8,f28,f81,f85
  f83: cylinder r=0.79mm len=15.08mm, axis (0,0,-1), area 18.8mm2, adj f3,f8,f11,f86
  f84: cylinder r=0.79mm len=42.95mm, axis (0,1,0), area 53.3mm2, adj f0,f11,f17,f86
  f85: cylinder r=0.79mm len=97.16mm, axis (-1,0,0), area 119.9mm2, adj f4,f8,f82,f87
  f86: sphere r=0.79mm, area 1mm2, adj f83,f84,f88
  f87: cylinder r=0.79mm len=11.11mm, axis (0,0,-1), area 13.2mm2, adj f2,f8,f85,f89
  f88: cylinder r=0.79mm len=28.26mm, axis (-1,0,0), area 35.2mm2, adj f0,f8,f86,f89
  f89: sphere r=0.79mm, area 1mm2, adj f87,f88,f90
  f90: cylinder r=0.79mm len=2.65mm, axis (0,1,0), area 2.9mm2, adj f0,f2,f89,f91
  f91: cylinder r=0.79mm len=27.78mm, axis (-1,0,0), area 33.6mm2, adj f0,f41,f90,f92
  f92: cylinder r=0.79mm len=8.19mm, axis (0,1,0), area 9mm2, adj f0,f43,f91,f93
  f93: cylinder r=0.79mm len=27.78mm, axis (1,0,0), area 33.6mm2, adj f0,f42,f92,f94
  f94: cylinder r=0.79mm len=3.45mm, axis (0,1,0), area 3.6mm2, adj f0,f2,f93,f95
  f95: cylinder r=0.79mm len=27.78mm, axis (-1,0,0), area 33.6mm2, adj f0,f38,f94,f96
  f96: cylinder r=0.79mm len=8.19mm, axis (0,1,0), area 9mm2, adj f0,f40,f95,f97
  f97: cylinder r=0.79mm len=27.78mm, axis (1,0,0), area 33.6mm2, adj f0,f39,f96,f98
  f98: cylinder r=0.79mm len=3.45mm, axis (0,1,0), area 3.6mm2, adj f0,f2,f97,f99
  f99: cylinder r=0.79mm len=27.78mm, axis (-1,0,0), area 33.6mm2, adj f0,f29,f98,f100
  f100: cylinder r=0.79mm len=8.19mm, axis (0,1,0), area 9mm2, adj f0,f31,f99,f101
  f101: cylinder r=0.79mm len=27.78mm, axis (1,0,0), area 33.6mm2, adj f0,f30,f100,f102
  f102: cylinder r=0.79mm len=3.45mm, axis (0,1,0), area 3.6mm2, adj f0,f2,f101,f103
  f103: cylinder r=0.79mm len=27.78mm, axis (-1,0,0), area 33.6mm2, adj f0,f32,f102,f104
  f104: cylinder r=0.79mm len=8.19mm, axis (0,1,0), area 9mm2, adj f0,f34,f103,f105
  f105: cylinder r=0.79mm len=27.78mm, axis (1,0,0), area 33.6mm2, adj f0,f33,f104,f106
  f106: cylinder r=0.79mm len=3.45mm, axis (0,1,0), area 3.6mm2, adj f0,f2,f105,f107
  f107: cylinder r=0.79mm len=27.78mm, axis (-1,0,0), area 33.6mm2, adj f0,f35,f106,f108
  f108: cylinder r=0.79mm len=8.19mm, axis (0,1,0), area 9mm2, adj f0,f37,f107,f109
  f109: cylinder r=0.79mm len=27.78mm, axis (1,0,0), area 33.6mm2, adj f0,f36,f108,f110
  f110: cylinder r=0.79mm len=3.45mm, axis (0,1,0), area 3.6mm2, adj f0,f2,f109,f113
  f111: cylinder r=0.79mm len=13.2mm, axis (0,1,0), area 15.6mm2, adj f0,f11,f15,f114
  f112: cylinder r=0.79mm len=15.08mm, axis (0,0,1), area 18.8mm2, adj f3,f11,f13,f114
  f113: cylinder r=0.79mm len=27.78mm, axis (-1,0,0), area 33.6mm2, adj f0,f27,f110,f115
  f114: sphere r=0.79mm, area 1mm2, adj f111,f112,f116
  f115: cylinder r=0.79mm len=10.05mm, axis (0,1,0), area 11.9mm2, adj f0,f26,f113,f117
  f116: cylinder r=0.79mm len=1.27mm, axis (1,0,0), area 1.6mm2, adj f0,f13,f114,f117
  f117: sphere r=0.79mm, area 1mm2, adj f115,f116,f118
  f118: cylinder r=0.79mm len=7.71mm, axis (0,0,1), area 7.6mm2, adj f13,f26,f68,f117
  f119: cylinder r=0.79mm len=26.99mm, axis (1,0,0), area 49.1mm2, adj f1,f2,f9,f10,f26,f68
PLACE A rot(axis=(1,0,0),0.1deg) t=(0.25,0.01,-0.03)mm
PLACE B at identity fixed
MATE revolute B.f5 <-> A.f30  axis (-1,0,0) through (-61.09,23.94,7.94)mm
